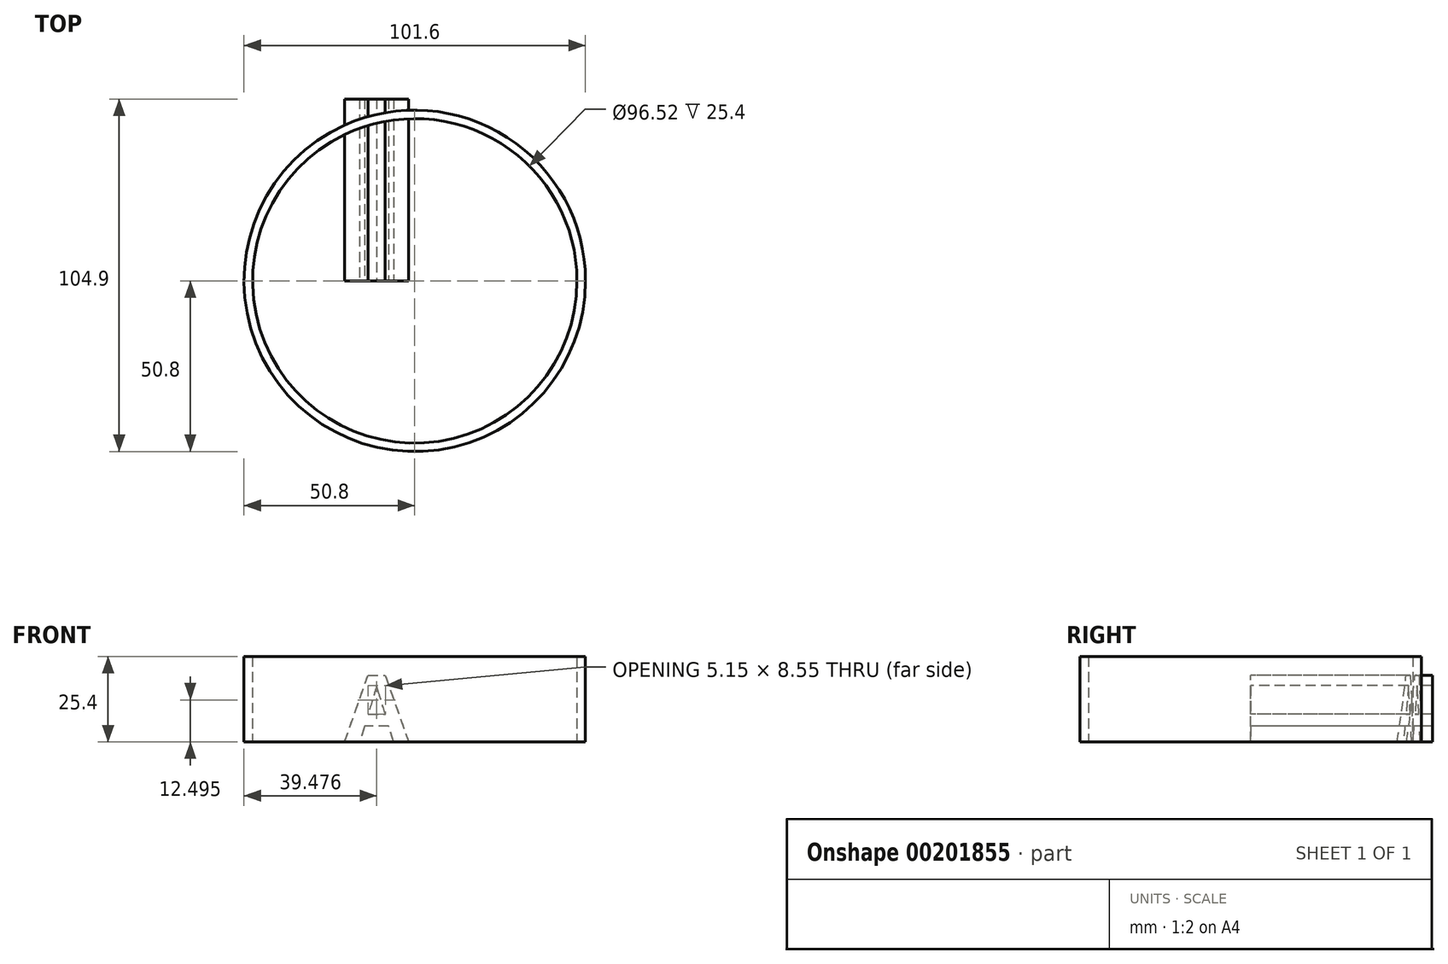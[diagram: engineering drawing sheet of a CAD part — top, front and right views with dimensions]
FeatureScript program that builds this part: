
annotation { "Feature Type Name" : "Feature", "Feature Type Description" : "" }
export const myFeature = defineFeature(function(context is Context, id is Id, definition is map)
    precondition{}
    {
        {
            var Q0;
            Q0=qCreatedBy(makeId("Top.planeOp"),FACE);
            var sketch = newSketch(context, id + "F0", { "sketchPlane" : qUnion([Q0])});
            skCircle(sketch, "E0", {"center": v(0, 0) * mm, "radius": 50.8 * mm});
            skSolve(sketch);
        }
        {
            var Q0;
            Q0=makeQuery(id+"F0.imprint","IMPRINT",FACE,{"disambiguationData":[TD([[makeQuery(id+"F0.imprint","IMPRINT",EDGE,{"derivedFrom":sQuery(id+"F0.wireOp",EDGE,"E0")}),1.0]])]});
            extrude(context, id + "F1", {"entities" : qUnion([Q0]), "depth" : 25.4 * mm});
        }
        {
            var Q0;
            Q0=makeQuery(id+"F1.opExtrude","CAP_FACE",FACE,{"disambiguationData":[OSD([sQuery(id+"F0.wireOp",EDGE,"E0")])],"isStart":true});
            var sketch = newSketch(context, id + "F2", { "sketchPlane" : qUnion([Q0])});
            skPoint(sketch, "E1", {"position": v(0, 0) * mm});
            skSolve(sketch);
        }
        {
            var Q0;
            Q0=sQuery(id+"F2.wireOp",VERTEX,"E1");
            var Q1;
            Q1=makeQuery(id+"F1.opExtrude","SWEPT_BODY",BODY,{"disambiguationData":[OSD([sQuery(id+"F0.wireOp",EDGE,"E0")])]});
            hole(context, id + "F3", {"style" : HoleStyle.SIMPLE, "endStyle" : HoleEndStyle.THROUGH, "holeDiameter" : 96.52 * mm, "locations" : qUnion([Q0]), "scope" : qUnion([Q1]), "isTappedThrough" : true});
        }
        {
            var Q0;
            Q0=qCreatedBy(makeId("Front.planeOp"),FACE);
            var sketch = newSketch(context, id + "F4", { "sketchPlane" : qUnion([Q0])});
            skText(sketch, "E2", { "text": "A", "fontName": "OpenSans-Bold.ttf"});
            const initialGuessF4  = {"E2": [-0.0209, 0, 1, 0, 0.01993]};
            skSetInitialGuess(sketch, initialGuessF4);
            skSolve(sketch);
        }
        {
            var Q0;
            Q0 = qSketchRegion(id + "F4", true);
            extrude(context, id + "F5", {"entities" : qUnion([Q0]), "operationType" : NewBodyOperationType.ADD, "oppositeDirection" : true, "depth" : 54.1 * mm});
        }
    });
